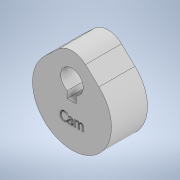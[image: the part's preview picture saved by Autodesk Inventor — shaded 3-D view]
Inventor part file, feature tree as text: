
AUTODESK INVENTOR PART (.ipt)
format: ipt  version: 2021 (Build 250183000, 183)  size: 247,808 bytes
history: native  units: mm
features: sketch x2, extrude x1, emboss x1
ambient origin geometry x8: Origin, YZ Plane, XZ Plane, XY Plane, X Axis, Y Axis, Z Axis, Center Point
bodies: Solid1 (feature_tree)
feature tree (4):
  extrude  "Extrusion1"  Depth=6.0mm
  emboss  "Emboss1"
  sketch  "Sketch1"  dims[d0=17.5mm d1=6.0mm]
  sketch  "Sketch2"  dims[d2=8.75mm d3=5.0mm d4=4.5mm d5=8.0mm d6=0.0mm d7=2.0mm d8=1.5mm d9=1.0mm d10=0.0mm]
